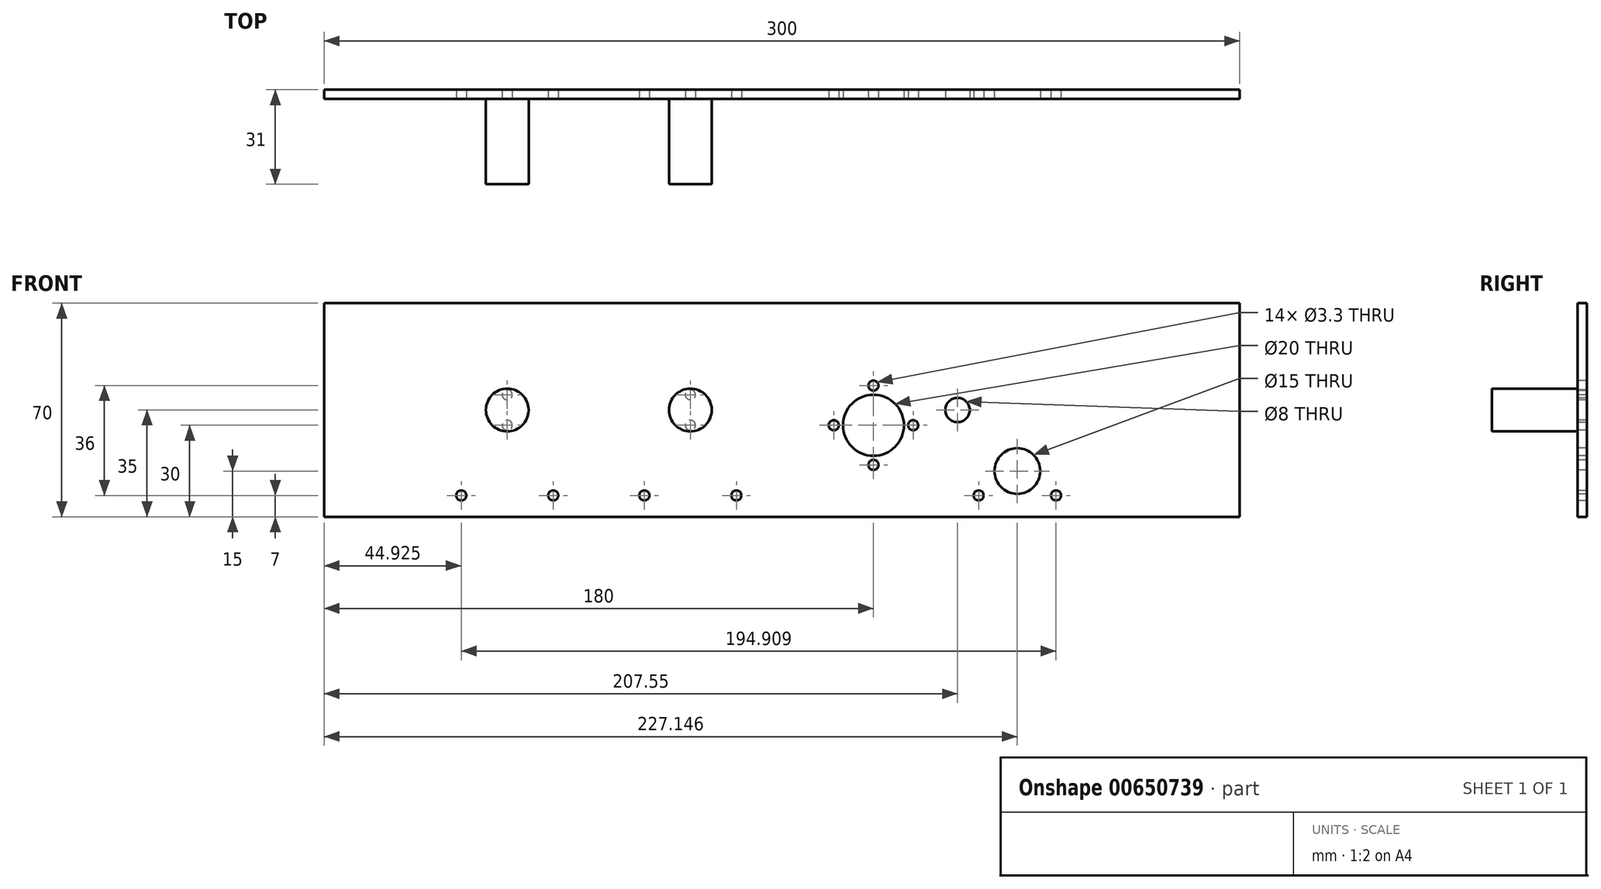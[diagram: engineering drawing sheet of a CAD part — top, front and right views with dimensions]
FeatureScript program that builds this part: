
annotation { "Feature Type Name" : "Feature", "Feature Type Description" : "" }
export const myFeature = defineFeature(function(context is Context, id is Id, definition is map)
    precondition{}
    {
        {
            var Q0;
            Q0=qCreatedBy(makeId("Front.planeOp"),FACE);
            var sketch = newSketch(context, id + "F0", { "sketchPlane" : qUnion([Q0])});
            skLineSegment(sketch, "E0.bottom", {"start": v(0, 0) * mm, "end": v(300, 0) * mm});
            skLineSegment(sketch, "E0.top", {"start": v(0, 70) * mm, "end": v(300, 70) * mm});
            skLineSegment(sketch, "E0.left", {"start": v(0, 0) * mm, "end": v(0, 70) * mm});
            skLineSegment(sketch, "E0.right", {"start": v(300, 0) * mm, "end": v(300, 70) * mm});
            skSolve(sketch);
        }
        {
            var Q0;
            Q0 = qSketchRegion(id + "F0", true);
            extrude(context, id + "F1", {"entities" : qUnion([Q0]), "depth" : 3 * mm, "offsetDistance" : 25 * mm});
        }
        {
            var Q0;
            Q0=makeQuery(id+"F1.opExtrude","CAP_FACE",FACE,{"disambiguationData":[OSD([sQuery(id+"F0.wireOp",EDGE,"E0.bottom"),sQuery(id+"F0.wireOp",EDGE,"E0.top"),sQuery(id+"F0.wireOp",EDGE,"E0.left"),sQuery(id+"F0.wireOp",EDGE,"E0.right")])],"isStart":false});
            var sketch = newSketch(context, id + "F2", { "sketchPlane" : qUnion([Q0])});
            skPoint(sketch, "E1", {"position": v(60, 35) * mm});
            skPoint(sketch, "E2", {"position": v(120, 35) * mm});
            skPoint(sketch, "E3", {"position": v(60, 40) * mm});
            skPoint(sketch, "E4", {"position": v(60, 30) * mm});
            skPoint(sketch, "E5", {"position": v(120, 30) * mm});
            skPoint(sketch, "E6", {"position": v(120, 40) * mm});
            skSolve(sketch);
        }
        {
            var Q0;
            Q0=sQuery(id+"F2.wireOp",VERTEX,"E3");
            var Q1;
            Q1=sQuery(id+"F2.wireOp",VERTEX,"E4");
            var Q2;
            Q2=sQuery(id+"F2.wireOp",VERTEX,"E6");
            var Q3;
            Q3=sQuery(id+"F2.wireOp",VERTEX,"E5");
            var Q4;
            Q4=makeQuery(id+"F1.opExtrude","SWEPT_BODY",BODY,{"disambiguationData":[OSD([sQuery(id+"F0.wireOp",EDGE,"E0.bottom"),sQuery(id+"F0.wireOp",EDGE,"E0.top"),sQuery(id+"F0.wireOp",EDGE,"E0.left"),sQuery(id+"F0.wireOp",EDGE,"E0.right")])]});
            hole(context, id + "F3", {"style" : HoleStyle.SIMPLE, "endStyle" : HoleEndStyle.THROUGH, "standardTappedOrClearance" : lookupTablePath({ "standard" : "ISO", "fit" : "Normal", "size" : "M3", "type" : "Clearance" }), "standardBlindInLast" : lookupTablePath({ "fit" : "Standard", "standard" : "ISO", "size" : "M3", "type" : "Clearance" }), "holeDiameter" : 3.3 * mm, "majorDiameter" : 3 * mm, "isTappedThrough" : true, "tappedDepth" : 5.5 * mm, "tapClearance" : 3, "locations" : qUnion([Q0, Q1, Q2, Q3]), "scope" : qUnion([Q4])});
        }
        {
            var Q0;
            Q0=makeQuery(id+"F1.opExtrude","CAP_FACE",FACE,{"disambiguationData":[OSD([sQuery(id+"F0.wireOp",EDGE,"E0.bottom"),sQuery(id+"F0.wireOp",EDGE,"E0.top"),sQuery(id+"F0.wireOp",EDGE,"E0.left"),sQuery(id+"F0.wireOp",EDGE,"E0.right")])],"isStart":false});
            var sketch = newSketch(context, id + "F4", { "sketchPlane" : qUnion([Q0])});
            skCircle(sketch, "E7", {"center": v(60, 35) * mm, "radius": 7 * mm});
            skCircle(sketch, "E8", {"center": v(120, 35) * mm, "radius": 7 * mm});
            skCircle(sketch, "E9.0", {"center": v(60, 40) * mm, "radius": 1.65 * mm});
            skCircle(sketch, "E10.0", {"center": v(60, 30) * mm, "radius": 1.65 * mm});
            skCircle(sketch, "E11.0", {"center": v(120, 30) * mm, "radius": 1.65 * mm});
            skCircle(sketch, "E12.0", {"center": v(120, 40) * mm, "radius": 1.65 * mm});
            skLineSegment(sketch, "E13", {"start": v(60, 40) * mm, "end": v(60, 30) * mm, "construction": true});
            skLineSegment(sketch, "E14", {"start": v(120, 40) * mm, "end": v(120, 30) * mm, "construction": true});
            skSolve(sketch);
        }
        {
            var Q0;
            Q0 = qSketchRegion(id + "F4", true);
            var Q1;
            Q1=makeQuery(id+"F4.imprint","IMPRINT",FACE,{"disambiguationData":[TD([[makeQuery(id+"F4.imprint","IMPRINT",EDGE,{"derivedFrom":sQuery(id+"F4.wireOp",EDGE,"E9.0")}),1.0]])]});
            var Q2;
            Q2=makeQuery(id+"F4.imprint","IMPRINT",FACE,{"disambiguationData":[TD([[makeQuery(id+"F4.imprint","IMPRINT",EDGE,{"derivedFrom":sQuery(id+"F4.wireOp",EDGE,"E10.0")}),1.0]])]});
            var Q3;
            Q3=makeQuery(id+"F4.imprint","IMPRINT",FACE,{"disambiguationData":[TD([[makeQuery(id+"F4.imprint","IMPRINT",EDGE,{"derivedFrom":sQuery(id+"F4.wireOp",EDGE,"E12.0")}),1.0]])]});
            var Q4;
            Q4=makeQuery(id+"F4.imprint","IMPRINT",FACE,{"disambiguationData":[TD([[makeQuery(id+"F4.imprint","IMPRINT",EDGE,{"derivedFrom":sQuery(id+"F4.wireOp",EDGE,"E11.0")}),1.0]])]});
            extrude(context, id + "F5", {"entities" : qUnion([Q0, Q1, Q2, Q3, Q4]), "depth" : 28 * mm, "offsetDistance" : 25 * mm});
        }
        {
            var Q0;
            Q0=makeQuery(id+"F1.opExtrude","CAP_FACE",FACE,{"disambiguationData":[OSD([sQuery(id+"F0.wireOp",EDGE,"E0.bottom"),sQuery(id+"F0.wireOp",EDGE,"E0.top"),sQuery(id+"F0.wireOp",EDGE,"E0.left"),sQuery(id+"F0.wireOp",EDGE,"E0.right")])],"isStart":false});
            var sketch = newSketch(context, id + "F6", { "sketchPlane" : qUnion([Q0])});
            skPoint(sketch, "E15", {"position": v(60, 35) * mm});
            skPoint(sketch, "E16", {"position": v(120, 35) * mm});
            skLineSegment(sketch, "E17", {"start": v(60, 40) * mm, "end": v(60, 30) * mm, "construction": true});
            skLineSegment(sketch, "E18", {"start": v(120, 40) * mm, "end": v(120, 30) * mm, "construction": true});
            skCircle(sketch, "E19", {"center": v(180, 30) * mm, "radius": 13 * mm, "construction": true});
            skPoint(sketch, "E20", {"position": v(180, 43) * mm});
            skPoint(sketch, "E21", {"position": v(180, 17) * mm});
            skPoint(sketch, "E22", {"position": v(193, 30) * mm});
            skPoint(sketch, "E23", {"position": v(167, 30) * mm});
            skSolve(sketch);
        }
        {
            var Q0;
            Q0=sQuery(id+"F6.wireOp",VERTEX,"E23");
            var Q1;
            Q1=sQuery(id+"F6.wireOp",VERTEX,"E20");
            var Q2;
            Q2=sQuery(id+"F6.wireOp",VERTEX,"E22");
            var Q3;
            Q3=sQuery(id+"F6.wireOp",VERTEX,"E21");
            var Q4;
            Q4=makeQuery(id+"F1.opExtrude","SWEPT_BODY",BODY,{"disambiguationData":[OSD([sQuery(id+"F0.wireOp",EDGE,"E0.bottom"),sQuery(id+"F0.wireOp",EDGE,"E0.top"),sQuery(id+"F0.wireOp",EDGE,"E0.left"),sQuery(id+"F0.wireOp",EDGE,"E0.right")])]});
            hole(context, id + "F7", {"style" : HoleStyle.SIMPLE, "endStyle" : HoleEndStyle.THROUGH, "standardTappedOrClearance" : lookupTablePath({ "standard" : "ISO", "fit" : "Normal", "size" : "M3", "type" : "Clearance" }), "standardBlindInLast" : lookupTablePath({ "fit" : "Standard", "standard" : "ISO", "size" : "M3", "type" : "Clearance" }), "holeDiameter" : 3.3 * mm, "majorDiameter" : 3 * mm, "isTappedThrough" : true, "tappedDepth" : 5.5 * mm, "tapClearance" : 3, "locations" : qUnion([Q0, Q1, Q2, Q3]), "scope" : qUnion([Q4])});
        }
        {
            var Q0;
            Q0=makeQuery(id+"F1.opExtrude","CAP_FACE",FACE,{"disambiguationData":[OSD([sQuery(id+"F0.wireOp",EDGE,"E0.bottom"),sQuery(id+"F0.wireOp",EDGE,"E0.top"),sQuery(id+"F0.wireOp",EDGE,"E0.left"),sQuery(id+"F0.wireOp",EDGE,"E0.right")])],"isStart":false});
            var sketch = newSketch(context, id + "F8", { "sketchPlane" : qUnion([Q0])});
            skLineSegment(sketch, "E24", {"start": v(167, 30) * mm, "end": v(193, 30) * mm, "construction": true});
            skLineSegment(sketch, "E25", {"start": v(180, 43) * mm, "end": v(180, 17) * mm, "construction": true});
            skCircle(sketch, "E26", {"center": v(180, 30) * mm, "radius": 10 * mm});
            skSolve(sketch);
        }
        {
            var Q0;
            Q0=makeQuery(id+"F8.imprint","IMPRINT",FACE,{"disambiguationData":[TD([[makeQuery(id+"F8.imprint","IMPRINT",EDGE,{"derivedFrom":sQuery(id+"F8.wireOp",EDGE,"E26")}),1.0]])]});
            extrude(context, id + "F9", {"entities" : qUnion([Q0]), "operationType" : NewBodyOperationType.REMOVE, "endBound" : BoundingType.THROUGH_ALL, "oppositeDirection" : true, "depth" : 25 * mm, "offsetDistance" : 25 * mm});
        }
        {
            var Q0;
            Q0=makeQuery(id+"F1.opExtrude","CAP_FACE",FACE,{"disambiguationData":[OSD([sQuery(id+"F0.wireOp",EDGE,"E0.bottom"),sQuery(id+"F0.wireOp",EDGE,"E0.top"),sQuery(id+"F0.wireOp",EDGE,"E0.left"),sQuery(id+"F0.wireOp",EDGE,"E0.right")])],"isStart":false});
            var sketch = newSketch(context, id + "F10", { "sketchPlane" : qUnion([Q0])});
            skCircle(sketch, "E27", {"center": v(207.55, 35) * mm, "radius": 4 * mm});
            skCircle(sketch, "E28", {"center": v(180, 30) * mm, "radius": 28 * mm, "construction": true});
            skCircle(sketch, "E29", {"center": v(207.55, 35) * mm, "radius": 28 * mm, "construction": true});
            skCircle(sketch, "E30", {"center": v(227.15, 15) * mm, "radius": 7.5 * mm});
            skSolve(sketch);
        }
        {
            var Q0;
            Q0 = qSketchRegion(id + "F10", true);
            extrude(context, id + "F11", {"entities" : qUnion([Q0]), "operationType" : NewBodyOperationType.REMOVE, "endBound" : BoundingType.THROUGH_ALL, "oppositeDirection" : true, "depth" : 25 * mm, "offsetDistance" : 25 * mm});
        }
        {
            var Q0;
            Q0=makeQuery(id+"F1.opExtrude","CAP_FACE",FACE,{"disambiguationData":[OSD([sQuery(id+"F0.wireOp",EDGE,"E0.bottom"),sQuery(id+"F0.wireOp",EDGE,"E0.top"),sQuery(id+"F0.wireOp",EDGE,"E0.left"),sQuery(id+"F0.wireOp",EDGE,"E0.right")])],"isStart":false});
            var sketch = newSketch(context, id + "F12", { "sketchPlane" : qUnion([Q0])});
            skPoint(sketch, "E31", {"position": v(104.93, 7) * mm});
            skPoint(sketch, "E32", {"position": v(239.83, 7) * mm});
            skPoint(sketch, "E33", {"position": v(44.93, 7) * mm});
            skLineSegment(sketch, "E34", {"start": v(44.93, 7) * mm, "end": v(239.83, 7) * mm, "construction": true});
            skCircle(sketch, "E35", {"center": v(60, 30) * mm, "radius": 27.5 * mm, "construction": true});
            skCircle(sketch, "E36", {"center": v(120, 30) * mm, "radius": 27.5 * mm, "construction": true});
            skPoint(sketch, "E37", {"position": v(75.07, 7) * mm});
            skPoint(sketch, "E38", {"position": v(135.07, 7) * mm});
            skPoint(sketch, "E39", {"position": v(214.46, 7) * mm});
            skCircle(sketch, "E40", {"center": v(227.15, 15) * mm, "radius": 15 * mm, "construction": true});
            skSolve(sketch);
        }
        {
            var Q0;
            Q0=sQuery(id+"F12.wireOp",VERTEX,"E33");
            var Q1;
            Q1=sQuery(id+"F12.wireOp",VERTEX,"E37");
            var Q2;
            Q2=sQuery(id+"F12.wireOp",VERTEX,"E31");
            var Q3;
            Q3=sQuery(id+"F12.wireOp",VERTEX,"E38");
            var Q4;
            Q4=sQuery(id+"F12.wireOp",VERTEX,"E39");
            var Q5;
            Q5=sQuery(id+"F12.wireOp",VERTEX,"E32");
            var Q6;
            Q6=makeQuery(id+"F1.opExtrude","SWEPT_BODY",BODY,{"disambiguationData":[OSD([sQuery(id+"F0.wireOp",EDGE,"E0.bottom"),sQuery(id+"F0.wireOp",EDGE,"E0.top"),sQuery(id+"F0.wireOp",EDGE,"E0.left"),sQuery(id+"F0.wireOp",EDGE,"E0.right")])]});
            hole(context, id + "F13", {"style" : HoleStyle.SIMPLE, "endStyle" : HoleEndStyle.THROUGH, "standardTappedOrClearance" : lookupTablePath({ "standard" : "ISO", "fit" : "Normal", "size" : "M3", "type" : "Clearance" }), "standardBlindInLast" : lookupTablePath({ "fit" : "Standard", "standard" : "ISO", "size" : "M3", "type" : "Clearance" }), "holeDiameter" : 3.3 * mm, "majorDiameter" : 5 * mm, "isTappedThrough" : true, "tappedDepth" : 5.5 * mm, "tapClearance" : 3, "locations" : qUnion([Q0, Q1, Q2, Q3, Q4, Q5]), "scope" : qUnion([Q6])});
        }
    });
